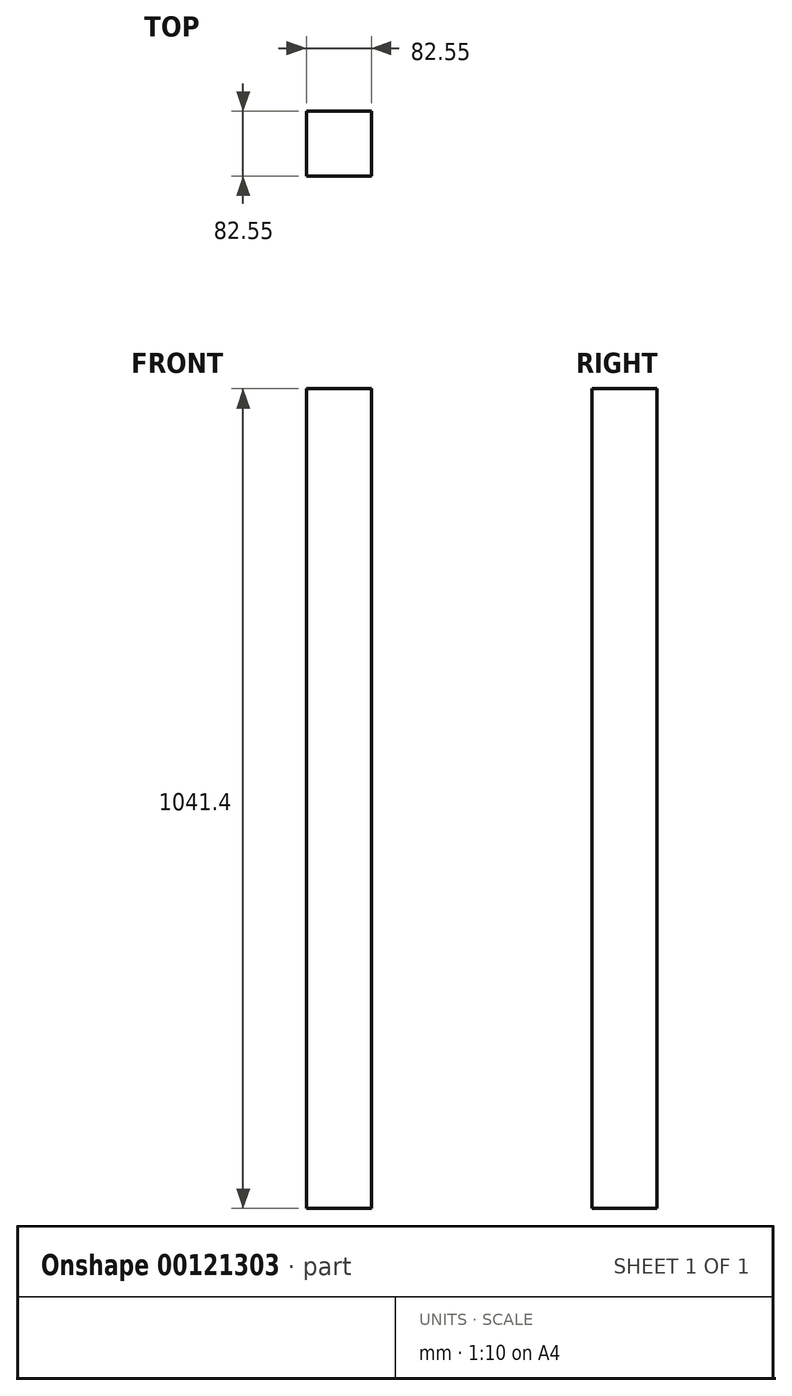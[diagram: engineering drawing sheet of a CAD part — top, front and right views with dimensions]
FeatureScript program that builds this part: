
annotation { "Feature Type Name" : "Feature", "Feature Type Description" : "" }
export const myFeature = defineFeature(function(context is Context, id is Id, definition is map)
    precondition{}
    {
        {
            var Q0;
            Q0=qCreatedBy(makeId("Top.planeOp"),FACE);
            var sketch = newSketch(context, id + "F0", { "sketchPlane" : qUnion([Q0])});
            skLineSegment(sketch, "E0.bottom", {"start": v(0, 0) * mm, "end": v(82.55, 0) * mm});
            skLineSegment(sketch, "E0.top", {"start": v(0, 82.55) * mm, "end": v(82.55, 82.55) * mm});
            skLineSegment(sketch, "E0.left", {"start": v(0, 0) * mm, "end": v(0, 82.55) * mm});
            skLineSegment(sketch, "E0.right", {"start": v(82.55, 0) * mm, "end": v(82.55, 82.55) * mm});
            skSolve(sketch);
        }
        {
            var Q0;
            Q0=makeQuery(id+"F0.imprint","IMPRINT",FACE,{"disambiguationData":[TD([[makeQuery(id+"F0.imprint","IMPRINT",EDGE,{"derivedFrom":sQuery(id+"F0.wireOp",EDGE,"E0.bottom")}),1.0]])]});
            extrude(context, id + "F1", {"entities" : qUnion([Q0]), "depth" : 1041.4 * mm});
        }
    });
